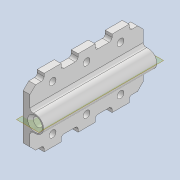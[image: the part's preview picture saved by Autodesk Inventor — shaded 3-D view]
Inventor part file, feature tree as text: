
AUTODESK INVENTOR PART (.ipt)
format: ipt  version: 2020 (Build 240168000, 168)  size: 212,992 bytes
history: native  units: mm
features: extrude x3, sketch x3, other x3, fillet x2, chamfer x2, projected_geometry x2, plane x1, mirror x1, reference x1
ambient origin geometry x8: Origin, YZ Plane, XZ Plane, XY Plane, X Axis, Y Axis, Z Axis, Center Point
bodies: Solid1 (feature_tree)
feature tree (18):
  extrude  "Extrusion1"  Depth=3.0mm
  fillet  "Fillet1"  Radius=1.2mm
  chamfer  "Chamfer1"  Distance=20.0mm
  extrude  "Extrusion2"  Depth=0.5mm TaperAngle=45.0deg
  extrude  "Extrusion3"  Depth=1.0mm
  plane  "Work Plane1"
  mirror  "Mirror1"
  fillet  "Fillet2"  Radius=4.0mm
  chamfer  "Chamfer2"  Distance=6.0mm
  sketch  "Sketch1"  dims[d0=1.6mm d1=3.0mm d2=1.2mm]
  reference  "Reference1"
  sketch  "Sketch2"  dims[d3=10.0mm d4=20.0mm d5=0.0mm]
  projected_geometry  "Projected Loop1"
  sketch  "Sketch3"  dims[d6=0.5mm d7=0.5mm d8=2.0mm d9=45.0deg d10=1.0mm d11=4.0mm d12=6.0mm d13=6.0mm d14=1.2mm d15=1.2mm d16=1.2mm d17=20.0mm d18=0.0mm d19=4.0mm d20=3.0mm d21=4.0mm d22=3.0mm d23=4.0mm d24=3.0mm d25=20.0mm d26=0.0mm d27=0.5mm d28=1.0mm d29=2.0mm d30=45.0deg]
  projected_geometry  "Projected Loop2"
  parser-record x1  (decoder bookkeeping rows leaked as tree rows — omitted from the tree; the rows remain in map.json)
  other  "bl_tube_ass_2.iam"
  other  "bw_tube_0.8_1.6:1"
note: 1 file-system path scrubbed to <path> (originals preserved in map.json)
